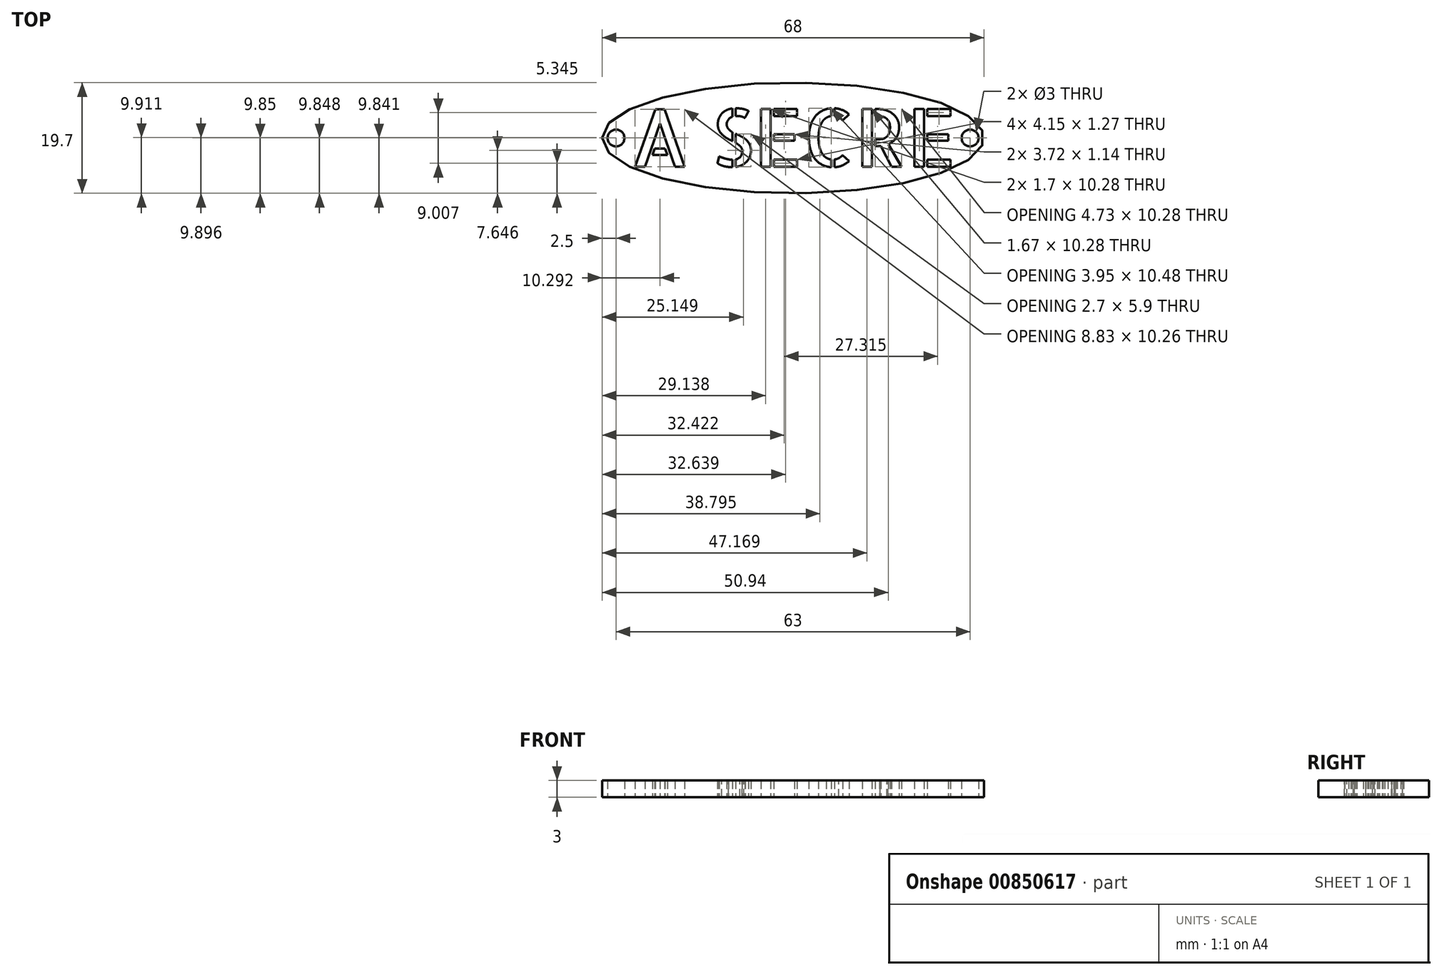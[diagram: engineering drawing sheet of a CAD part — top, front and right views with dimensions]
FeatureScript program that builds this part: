
annotation { "Feature Type Name" : "Feature", "Feature Type Description" : "" }
export const myFeature = defineFeature(function(context is Context, id is Id, definition is map)
    precondition{}
    {
        {
            var Q0;
            Q0=qCreatedBy(makeId("Top.planeOp"),FACE);
            var sketch = newSketch(context, id + "F0", { "sketchPlane" : qUnion([Q0])});
            skEllipse(sketch, "E0", {"center": v(0, 0) * mm, "majorRadius": 34 * mm, "minorRadius": 9.85 * mm, "majorAxis": v(-1, 0)});
            skCircle(sketch, "E1", {"center": v(-31.5, 0) * mm, "radius": 1.5 * mm});
            skCircle(sketch, "E2", {"center": v(31.5, 0) * mm, "radius": 1.5 * mm});
            skText(sketch, "E3", { "text": "A SECRE", "fontName": "AllertaStencil-Regular.ttf"});
            skLineSegment(sketch, "E4", {"start": v(-29, 0) * mm, "end": v(29, 0) * mm, "construction": true});
            const initialGuessF0  = {"E3": [-0.029, -0.00514, 1, 0, 0.01028]};
            skSetInitialGuess(sketch, initialGuessF0);
            skSolve(sketch);
        }
        {
            var Q0;
            Q0=makeQuery(id+"F0.imprint","IMPRINT",FACE,{"disambiguationData":[TD([[makeQuery(id+"F0.imprint","IMPRINT",EDGE,{"derivedFrom":sQuery(id+"F0.wireOp",EDGE,"E0")}),1.0]])]});
            extrude(context, id + "F1", {"entities" : qUnion([Q0]), "depth" : 3 * mm, "offsetDistance" : 25 * mm});
        }
    });
